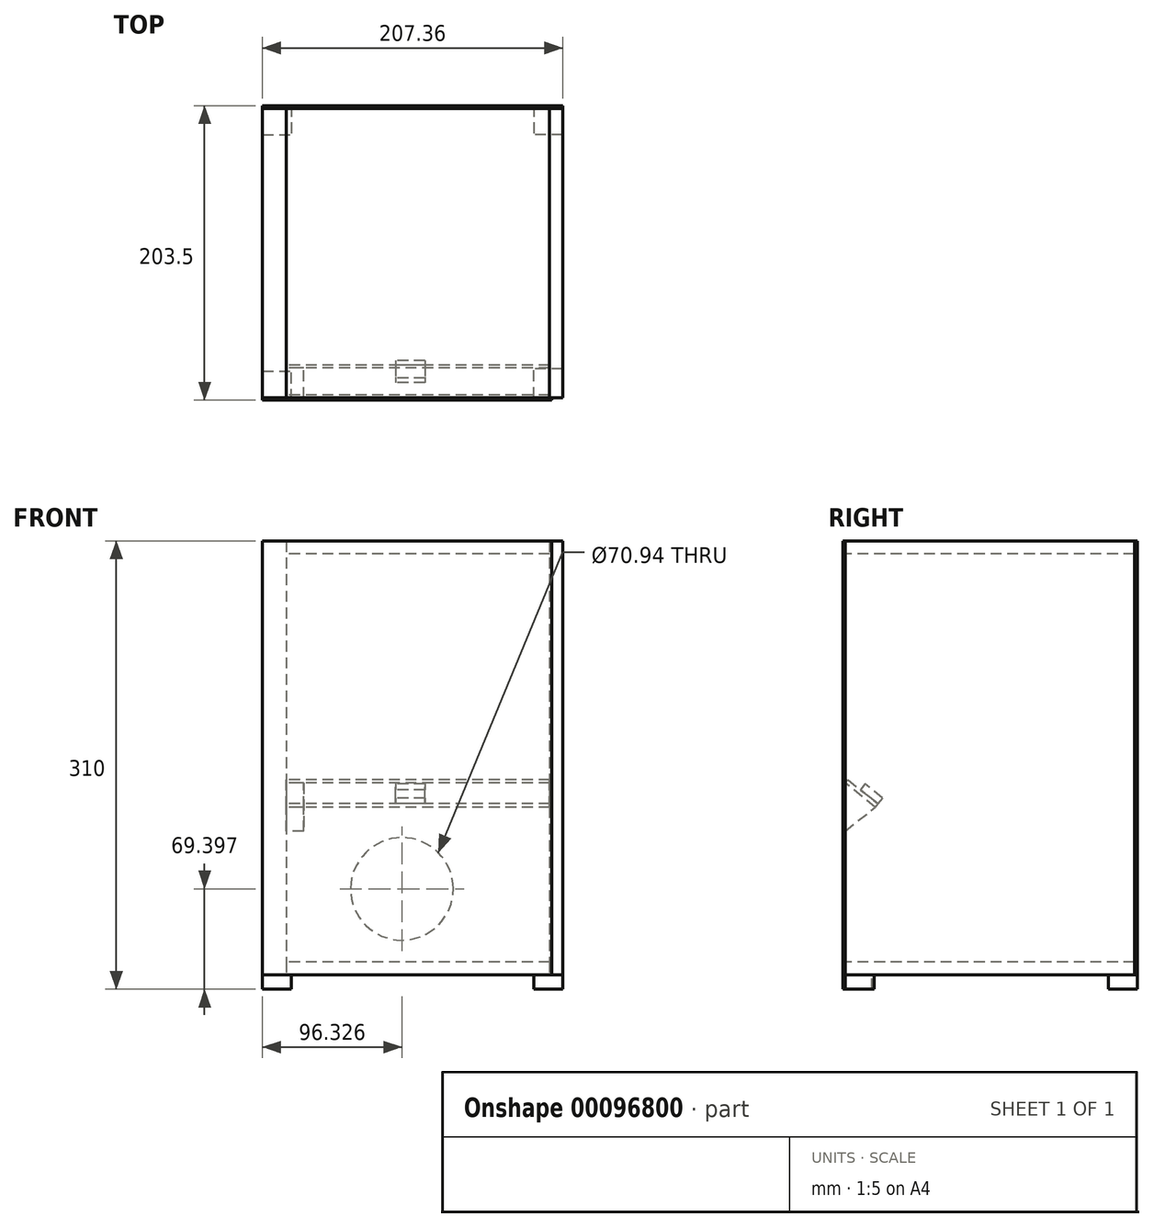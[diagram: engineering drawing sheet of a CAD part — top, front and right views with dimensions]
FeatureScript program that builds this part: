
annotation { "Feature Type Name" : "Feature", "Feature Type Description" : "" }
export const myFeature = defineFeature(function(context is Context, id is Id, definition is map)
    precondition{}
    {
        {
            var Q0;
            Q0=qCreatedBy(makeId("Front.planeOp"),FACE);
            var sketch = newSketch(context, id + "F0", { "sketchPlane" : qUnion([Q0])});
            skLineSegment(sketch, "E0.bottom", {"start": v(0, 0) * mm, "end": v(200, 0) * mm});
            skLineSegment(sketch, "E0.top", {"start": v(0, 300) * mm, "end": v(200, 300) * mm});
            skLineSegment(sketch, "E0.left", {"start": v(0, 0) * mm, "end": v(0, 300) * mm});
            skLineSegment(sketch, "E0.right", {"start": v(200, 0) * mm, "end": v(200, 300) * mm});
            skSolve(sketch);
        }
        {
            var Q0;
            Q0 = qSketchRegion(id + "F0", true);
            extrude(context, id + "F1", {"entities" : qUnion([Q0]), "depth" : 1.5 * mm});
        }
        {
            var Q0;
            Q0=makeQuery(id+"F1.opExtrude","CAP_FACE",FACE,{"disambiguationData":[OSD([sQuery(id+"F0.wireOp",EDGE,"E0.bottom"),sQuery(id+"F0.wireOp",EDGE,"E0.top"),sQuery(id+"F0.wireOp",EDGE,"E0.left"),sQuery(id+"F0.wireOp",EDGE,"E0.right")])],"isStart":true});
            var sketch = newSketch(context, id + "F2", { "sketchPlane" : qUnion([Q0])});
            skLineSegment(sketch, "E1.bottom", {"start": v(0, 300) * mm, "end": v(-16.36, 300) * mm});
            skLineSegment(sketch, "E1.top", {"start": v(0, 0) * mm, "end": v(-16.36, 0) * mm});
            skLineSegment(sketch, "E1.left", {"start": v(0, 300) * mm, "end": v(0, 0) * mm});
            skLineSegment(sketch, "E1.right", {"start": v(-16.36, 300) * mm, "end": v(-16.36, 0) * mm});
            skSolve(sketch);
        }
        {
            var Q0;
            Q0 = qSketchRegion(id + "F2", true);
            extrude(context, id + "F3", {"entities" : qUnion([Q0]), "depth" : 200 * mm});
        }
        {
            var Q0;
            Q0=makeQuery(id+"F3.opExtrude","SWEPT_FACE",FACE,{"disambiguationData":[OSD([sQuery(id+"F2.wireOp",EDGE,"E1.right")])]});
            var sketch = newSketch(context, id + "F4", { "sketchPlane" : qUnion([Q0])});
            skLineSegment(sketch, "E2", {"start": v(0, 132.67) * mm, "end": v(0, 99.28) * mm});
            skLineSegment(sketch, "E3", {"start": v(0, 99.28) * mm, "end": v(20.76, 115.98) * mm});
            skLineSegment(sketch, "E4", {"start": v(20.76, 115.98) * mm, "end": v(0, 132.67) * mm});
            skSolve(sketch);
        }
        {
            var Q0;
            Q0 = qSketchRegion(id + "F4", true);
            extrude(context, id + "F5", {"entities" : qUnion([Q0]), "depth" : 12 * mm});
        }
        {
            var Q0;
            Q0=makeQuery(id+"F3.opExtrude","SWEPT_FACE",FACE,{"disambiguationData":[OSD([sQuery(id+"F2.wireOp",EDGE,"E1.right")])]});
            var sketch = newSketch(context, id + "F6", { "sketchPlane" : qUnion([Q0])});
            skLineSegment(sketch, "E5", {"start": v(20.76, 115.98) * mm, "end": v(0, 132.57) * mm});
            skLineSegment(sketch, "E6", {"start": v(0, 132.57) * mm, "end": v(20.76, 115.98) * mm});
            skLineSegment(sketch, "E7", {"start": v(0, 132.57) * mm, "end": v(1.84, 134.88) * mm});
            skLineSegment(sketch, "E8", {"start": v(1.84, 134.88) * mm, "end": v(22.6, 118.28) * mm});
            skLineSegment(sketch, "E9", {"start": v(22.6, 118.28) * mm, "end": v(20.76, 115.98) * mm});
            skSolve(sketch);
        }
        {
            var Q0;
            Q0 = qSketchRegion(id + "F6", true);
            extrude(context, id + "F7", {"entities" : qUnion([Q0]), "depth" : 182 * mm});
        }
        {
            var Q0;
            Q0=makeQuery(id+"F7.opExtrude","SWEPT_FACE",FACE,{"disambiguationData":[OSD([sQuery(id+"F6.wireOp",EDGE,"E8")])]});
            var sketch = newSketch(context, id + "F8", { "sketchPlane" : qUnion([Q0])});
            skLineSegment(sketch, "E10.bottom", {"start": v(112.24, -56.2) * mm, "end": v(91.9, -56.2) * mm});
            skLineSegment(sketch, "E10.top", {"start": v(112.24, -71.74) * mm, "end": v(91.9, -71.74) * mm});
            skLineSegment(sketch, "E10.left", {"start": v(112.24, -56.2) * mm, "end": v(112.24, -71.74) * mm});
            skLineSegment(sketch, "E10.right", {"start": v(91.9, -56.2) * mm, "end": v(91.9, -71.74) * mm});
            skSolve(sketch);
        }
        {
            var Q0;
            Q0 = qSketchRegion(id + "F8", true);
            extrude(context, id + "F9", {"entities" : qUnion([Q0]), "depth" : 5 * mm});
        }
        {
            var Q0;
            Q0=makeQuery(id+"F3.opExtrude","SWEPT_FACE",FACE,{"disambiguationData":[OSD([sQuery(id+"F2.wireOp",EDGE,"E1.right")])]});
            var sketch = newSketch(context, id + "F10", { "sketchPlane" : qUnion([Q0])});
            skLineSegment(sketch, "E11.bottom", {"start": v(200, 300) * mm, "end": v(0, 300) * mm});
            skLineSegment(sketch, "E11.top", {"start": v(200, 291) * mm, "end": v(0, 291) * mm});
            skLineSegment(sketch, "E11.left", {"start": v(200, 300) * mm, "end": v(200, 291) * mm});
            skLineSegment(sketch, "E11.right", {"start": v(0, 300) * mm, "end": v(0, 291) * mm});
            skSolve(sketch);
        }
        {
            var Q0;
            Q0 = qSketchRegion(id + "F10", true);
            extrude(context, id + "F11", {"entities" : qUnion([Q0]), "depth" : 182 * mm});
        }
        {
            var Q0;
            Q0=makeQuery(id+"F3.opExtrude","SWEPT_FACE",FACE,{"disambiguationData":[OSD([sQuery(id+"F2.wireOp",EDGE,"E1.right")])]});
            var sketch = newSketch(context, id + "F12", { "sketchPlane" : qUnion([Q0])});
            skLineSegment(sketch, "E12.bottom", {"start": v(200, 0) * mm, "end": v(0, 0) * mm});
            skLineSegment(sketch, "E12.top", {"start": v(200, 9) * mm, "end": v(0, 9) * mm});
            skLineSegment(sketch, "E12.left", {"start": v(200, 0) * mm, "end": v(200, 9) * mm});
            skLineSegment(sketch, "E12.right", {"start": v(0, 0) * mm, "end": v(0, 9) * mm});
            skSolve(sketch);
        }
        {
            var Q0;
            Q0 = qSketchRegion(id + "F12", true);
            extrude(context, id + "F13", {"entities" : qUnion([Q0]), "depth" : 182 * mm});
        }
        {
            var Q0;
            Q0=makeQuery(id+"F11.opExtrude","CAP_FACE",FACE,{"disambiguationData":[OSD([sQuery(id+"F10.wireOp",EDGE,"E11.bottom"),sQuery(id+"F10.wireOp",EDGE,"E11.top"),sQuery(id+"F10.wireOp",EDGE,"E11.left"),sQuery(id+"F10.wireOp",EDGE,"E11.right")])],"isStart":false});
            var sketch = newSketch(context, id + "F14", { "sketchPlane" : qUnion([Q0])});
            skLineSegment(sketch, "E13.bottom", {"start": v(200, 300) * mm, "end": v(0, 300) * mm});
            skLineSegment(sketch, "E13.top", {"start": v(200, 0) * mm, "end": v(0, 0) * mm});
            skLineSegment(sketch, "E13.left", {"start": v(200, 300) * mm, "end": v(200, 0) * mm});
            skLineSegment(sketch, "E13.right", {"start": v(0, 300) * mm, "end": v(0, 0) * mm});
            skSolve(sketch);
        }
        {
            var Q0;
            Q0 = qSketchRegion(id + "F14", true);
            extrude(context, id + "F15", {"entities" : qUnion([Q0]), "depth" : 9 * mm});
        }
        {
            var Q0;
            Q0=makeQuery(id+"F15.opExtrude","SWEPT_FACE",FACE,{"disambiguationData":[OSD([sQuery(id+"F14.wireOp",EDGE,"E13.left")])]});
            var sketch = newSketch(context, id + "F16", { "sketchPlane" : qUnion([Q0])});
            skLineSegment(sketch, "E14.bottom", {"start": v(-207.36, 300) * mm, "end": v(0, 300) * mm});
            skLineSegment(sketch, "E14.top", {"start": v(-207.36, 0) * mm, "end": v(0, 0) * mm});
            skLineSegment(sketch, "E14.left", {"start": v(-207.36, 300) * mm, "end": v(-207.36, 0) * mm});
            skLineSegment(sketch, "E14.right", {"start": v(0, 300) * mm, "end": v(0, 0) * mm});
            skSolve(sketch);
        }
        {
            var Q0;
            Q0 = qSketchRegion(id + "F16", true);
            extrude(context, id + "F17", {"entities" : qUnion([Q0]), "depth" : 2 * mm});
        }
        {
            var Q0;
            Q0=makeQuery(id+"F17.opExtrude","CAP_FACE",FACE,{"disambiguationData":[OSD([sQuery(id+"F16.wireOp",EDGE,"E14.bottom"),sQuery(id+"F16.wireOp",EDGE,"E14.top"),sQuery(id+"F16.wireOp",EDGE,"E14.left"),sQuery(id+"F16.wireOp",EDGE,"E14.right")])],"isStart":false});
            var sketch = newSketch(context, id + "F18", { "sketchPlane" : qUnion([Q0])});
            skCircle(sketch, "E15", {"center": v(-96.33, 59.4) * mm, "radius": 35.47 * mm});
            skSolve(sketch);
        }
        {
            var Q0;
            Q0 = qSketchRegion(id + "F18", true);
            extrude(context, id + "F19", {"entities" : qUnion([Q0]), "operationType" : NewBodyOperationType.REMOVE, "oppositeDirection" : true, "depth" : 3 * mm});
        }
        {
            var Q0;
            Q0=makeQuery(id+"F3.opExtrude","SWEPT_FACE",FACE,{"disambiguationData":[OSD([sQuery(id+"F2.wireOp",EDGE,"E1.top")])]});
            var sketch = newSketch(context, id + "F20", { "sketchPlane" : qUnion([Q0])});
            skLineSegment(sketch, "E16.bottom", {"start": v(0, 1.5) * mm, "end": v(20, 1.5) * mm});
            skLineSegment(sketch, "E16.top", {"start": v(0, -18.5) * mm, "end": v(20, -18.5) * mm});
            skLineSegment(sketch, "E16.left", {"start": v(0, 1.5) * mm, "end": v(0, -18.5) * mm});
            skLineSegment(sketch, "E16.right", {"start": v(20, 1.5) * mm, "end": v(20, -18.5) * mm});
            skSolve(sketch);
        }
        {
            var Q0;
            Q0 = qSketchRegion(id + "F20", true);
            extrude(context, id + "F21", {"entities" : qUnion([Q0]), "depth" : 10 * mm});
        }
        {
            var Q0;
            Q0=makeQuery(id+"F15.opExtrude","SWEPT_FACE",FACE,{"disambiguationData":[OSD([sQuery(id+"F14.wireOp",EDGE,"E13.top")])]});
            var sketch = newSketch(context, id + "F22", { "sketchPlane" : qUnion([Q0])});
            skLineSegment(sketch, "E17.bottom", {"start": v(207.36, 0) * mm, "end": v(187.36, 0) * mm});
            skLineSegment(sketch, "E17.top", {"start": v(207.36, -20) * mm, "end": v(187.36, -20) * mm});
            skLineSegment(sketch, "E17.left", {"start": v(207.36, 0) * mm, "end": v(207.36, -20) * mm});
            skLineSegment(sketch, "E17.right", {"start": v(187.36, 0) * mm, "end": v(187.36, -20) * mm});
            skSolve(sketch);
        }
        {
            var Q0;
            Q0 = qSketchRegion(id + "F22", true);
            extrude(context, id + "F23", {"entities" : qUnion([Q0]), "depth" : 10 * mm});
        }
        {
            var Q0;
            Q0=makeQuery(id+"F3.opExtrude","SWEPT_FACE",FACE,{"disambiguationData":[OSD([sQuery(id+"F2.wireOp",EDGE,"E1.top")])]});
            var sketch = newSketch(context, id + "F24", { "sketchPlane" : qUnion([Q0])});
            skLineSegment(sketch, "E18.bottom", {"start": v(0, -202) * mm, "end": v(20, -202) * mm});
            skLineSegment(sketch, "E18.top", {"start": v(0, -182) * mm, "end": v(20, -182) * mm});
            skLineSegment(sketch, "E18.left", {"start": v(0, -202) * mm, "end": v(0, -182) * mm});
            skLineSegment(sketch, "E18.right", {"start": v(20, -202) * mm, "end": v(20, -182) * mm});
            skSolve(sketch);
        }
        {
            var Q0;
            Q0 = qSketchRegion(id + "F24", true);
            extrude(context, id + "F25", {"entities" : qUnion([Q0]), "depth" : 10 * mm});
        }
        {
            var Q0;
            Q0=makeQuery(id+"F17.opExtrude","SWEPT_FACE",FACE,{"disambiguationData":[OSD([sQuery(id+"F16.wireOp",EDGE,"E14.top")])]});
            var sketch = newSketch(context, id + "F26", { "sketchPlane" : qUnion([Q0])});
            skLineSegment(sketch, "E19.bottom", {"start": v(207.36, -202) * mm, "end": v(187.36, -202) * mm});
            skLineSegment(sketch, "E19.top", {"start": v(207.36, -182) * mm, "end": v(187.36, -182) * mm});
            skLineSegment(sketch, "E19.left", {"start": v(207.36, -202) * mm, "end": v(207.36, -182) * mm});
            skLineSegment(sketch, "E19.right", {"start": v(187.36, -202) * mm, "end": v(187.36, -182) * mm});
            skSolve(sketch);
        }
        {
            var Q0;
            Q0 = qSketchRegion(id + "F26", true);
            extrude(context, id + "F27", {"entities" : qUnion([Q0]), "depth" : 10 * mm});
        }
    });
